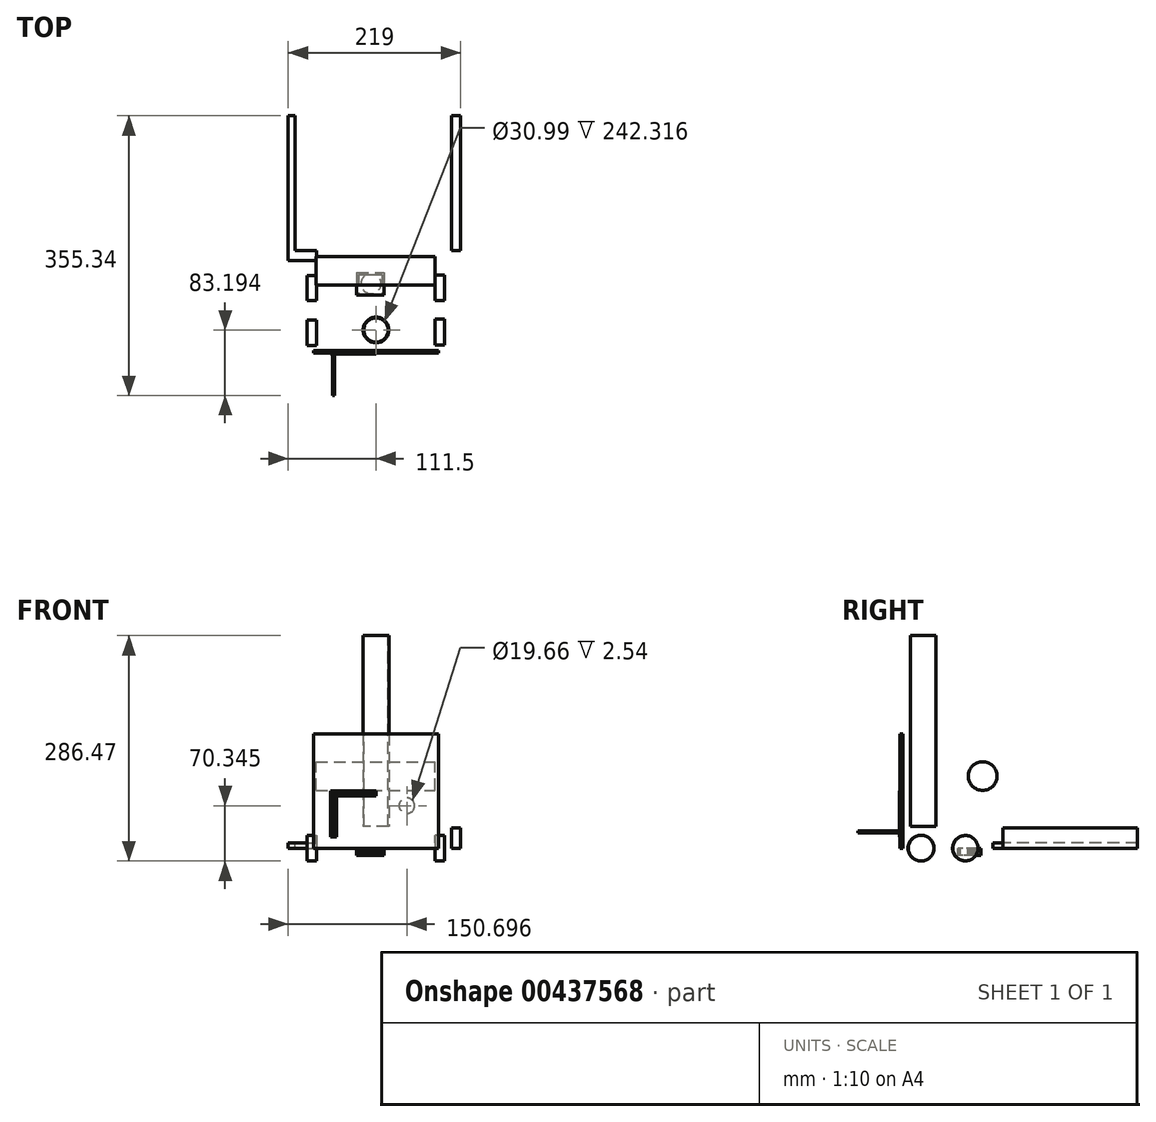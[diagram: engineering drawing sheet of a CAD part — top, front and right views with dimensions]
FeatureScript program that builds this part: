
annotation { "Feature Type Name" : "Feature", "Feature Type Description" : "" }
export const myFeature = defineFeature(function(context is Context, id is Id, definition is map)
    precondition{}
    {
        {
            var Q0;
            Q0=qCreatedBy(makeId("Front.planeOp"),FACE);
            var sketch = newSketch(context, id + "F0", { "sketchPlane" : qUnion([Q0])});
            skLineSegment(sketch, "E0.bottom", {"start": v(-79.55, 72.7) * mm, "end": v(79.55, 72.7) * mm});
            skLineSegment(sketch, "E0.top", {"start": v(-79.55, -72.7) * mm, "end": v(79.55, -72.7) * mm});
            skLineSegment(sketch, "E0.left", {"start": v(-79.55, 72.7) * mm, "end": v(-79.55, -72.7) * mm});
            skLineSegment(sketch, "E0.right", {"start": v(79.55, 72.7) * mm, "end": v(79.55, -72.7) * mm});
            skPoint(sketch, "E0.middle", {"position": v(0, 0) * mm});
            skSolve(sketch);
        }
        {
            var Q0;
            Q0=makeQuery(id+"F0.imprint","IMPRINT",FACE,{"disambiguationData":[TD([[makeQuery(id+"F0.imprint","IMPRINT",EDGE,{"derivedFrom":sQuery(id+"F0.wireOp",EDGE,"E0.bottom")}),-1.0]])]});
            extrude(context, id + "F1", {"entities" : qUnion([Q0]), "depth" : 3.56 * mm});
        }
        {
            var Q0;
            Q0=makeQuery(id+"F1.opExtrude","CAP_FACE",FACE,{"disambiguationData":[OSD([sQuery(id+"F0.wireOp",EDGE,"E0.bottom"),sQuery(id+"F0.wireOp",EDGE,"E0.top"),sQuery(id+"F0.wireOp",EDGE,"E0.left"),sQuery(id+"F0.wireOp",EDGE,"E0.right")])],"isStart":true});
            var sketch = newSketch(context, id + "F2", { "sketchPlane" : qUnion([Q0])});
            skLineSegment(sketch, "E1.bottom", {"start": v(-79.55, 72.7) * mm, "end": v(-74.99, 72.7) * mm});
            skLineSegment(sketch, "E1.top", {"start": v(-79.55, -72.7) * mm, "end": v(-74.99, -72.7) * mm});
            skLineSegment(sketch, "E1.left", {"start": v(-79.55, 72.7) * mm, "end": v(-79.55, -72.7) * mm});
            skLineSegment(sketch, "E1.right", {"start": v(-74.99, 72.7) * mm, "end": v(-74.99, -72.7) * mm});
            skSolve(sketch);
        }
        {
            var Q0;
            Q0=sQuery(id+"F2.wireOp",EDGE,"E1.right");
            extrude(context, id + "F3", {"bodyType" : ToolBodyType.SURFACE, "surfaceEntities" : qUnion([Q0]), "depth" : 127 * mm});
        }
        {
            var Q0;
            Q0=makeQuery(id+"F1.opExtrude","CAP_FACE",FACE,{"disambiguationData":[OSD([sQuery(id+"F0.wireOp",EDGE,"E0.bottom"),sQuery(id+"F0.wireOp",EDGE,"E0.top"),sQuery(id+"F0.wireOp",EDGE,"E0.left"),sQuery(id+"F0.wireOp",EDGE,"E0.right")])],"isStart":true});
            var sketch = newSketch(context, id + "F4", { "sketchPlane" : qUnion([Q0])});
            skLineSegment(sketch, "E2.bottom", {"start": v(79.55, 72.7) * mm, "end": v(75.43, 72.7) * mm});
            skLineSegment(sketch, "E2.top", {"start": v(79.55, -72.7) * mm, "end": v(75.43, -72.7) * mm});
            skLineSegment(sketch, "E2.left", {"start": v(79.55, 72.7) * mm, "end": v(79.55, -72.7) * mm});
            skLineSegment(sketch, "E2.right", {"start": v(75.43, 72.7) * mm, "end": v(75.43, -72.7) * mm});
            skSolve(sketch);
        }
        {
            var Q0;
            Q0=sQuery(id+"F4.wireOp",EDGE,"E2.right");
            extrude(context, id + "F5", {"bodyType" : ToolBodyType.SURFACE, "surfaceEntities" : qUnion([Q0]), "depth" : 127 * mm});
        }
        {
            var Q0;
            Q0=makeQuery(id+"F3.opExtrude","SWEPT_FACE",FACE,{"disambiguationData":[OSD([sQuery(id+"F2.wireOp",EDGE,"E1.right")])]});
            var sketch = newSketch(context, id + "F6", { "sketchPlane" : qUnion([Q0])});
            skCircle(sketch, "E3", {"center": v(101.22, 18.92) * mm, "radius": 18.2 * mm});
            skSolve(sketch);
        }
        {
            var Q0;
            Q0=makeQuery(id+"F6.imprint","IMPRINT",FACE,{"disambiguationData":[TD([[makeQuery(id+"F6.imprint","IMPRINT",EDGE,{"derivedFrom":sQuery(id+"F6.wireOp",EDGE,"E3")}),1.0]])]});
            extrude(context, id + "F7", {"entities" : qUnion([Q0]), "oppositeDirection" : true, "depth" : 151.38 * mm});
        }
        {
            var Q0;
            Q0=makeQuery(id+"F3.opExtrude","SWEPT_FACE",FACE,{"disambiguationData":[OSD([sQuery(id+"F2.wireOp",EDGE,"E1.right")])]});
            var sketch = newSketch(context, id + "F8", { "sketchPlane" : qUnion([Q0])});
            skLineSegment(sketch, "E4", {"start": v(127, -72.7) * mm, "end": v(55.42, -20.75) * mm});
            skSolve(sketch);
        }
        {
            var Q0;
            Q0=sQuery(id+"F8.wireOp",EDGE,"E4");
            extrude(context, id + "F9", {"bodyType" : ToolBodyType.SURFACE, "surfaceEntities" : qUnion([Q0]), "oppositeDirection" : true, "depth" : 150.11 * mm});
        }
        {
            var Q0;
            Q0=makeQuery(id+"F5.opExtrude","SWEPT_FACE",FACE,{"disambiguationData":[OSD([sQuery(id+"F4.wireOp",EDGE,"E2.right")])]});
            var sketch = newSketch(context, id + "F10", { "sketchPlane" : qUnion([Q0])});
            skLineSegment(sketch, "E5", {"start": v(88.54, -44.94) * mm, "end": v(0, -44.94) * mm});
            skSolve(sketch);
        }
        {
            var Q0;
            Q0=sQuery(id+"F10.wireOp",EDGE,"E5");
            extrude(context, id + "F11", {"bodyType" : ToolBodyType.SURFACE, "surfaceEntities" : qUnion([Q0]), "depth" : 143.5 * mm});
        }
        {
            var Q0;
            Q0=makeQuery(id+"F1.opExtrude","SWEPT_FACE",FACE,{"disambiguationData":[OSD([sQuery(id+"F0.wireOp",EDGE,"E0.top")])]});
            var sketch = newSketch(context, id + "F12", { "sketchPlane" : qUnion([Q0])});
            skLineSegment(sketch, "E6.bottom", {"start": v(79.55, 0) * mm, "end": v(-76.12, 0) * mm});
            skLineSegment(sketch, "E6.top", {"start": v(79.55, -126.38) * mm, "end": v(-76.12, -126.38) * mm});
            skLineSegment(sketch, "E6.left", {"start": v(79.55, 0) * mm, "end": v(79.55, -126.38) * mm});
            skLineSegment(sketch, "E6.right", {"start": v(-76.12, 0) * mm, "end": v(-76.12, -126.38) * mm});
            skSolve(sketch);
        }
        {
            var Q0;
            Q0=makeQuery(id+"F5.opExtrude","SWEPT_FACE",FACE,{"disambiguationData":[OSD([sQuery(id+"F4.wireOp",EDGE,"E2.right")])]});
            var sketch = newSketch(context, id + "F13", { "sketchPlane" : qUnion([Q0])});
            skLineSegment(sketch, "E7.bottom", {"start": v(127, -72.7) * mm, "end": v(114.2, -72.7) * mm});
            skLineSegment(sketch, "E7.top", {"start": v(127, -66.11) * mm, "end": v(114.2, -66.11) * mm});
            skLineSegment(sketch, "E7.left", {"start": v(127, -72.7) * mm, "end": v(127, -66.11) * mm});
            skLineSegment(sketch, "E7.right", {"start": v(114.2, -72.7) * mm, "end": v(114.2, -66.11) * mm});
            skSolve(sketch);
        }
        {
            var Q0;
            Q0=makeQuery(id+"F13.imprint","IMPRINT",FACE,{"disambiguationData":[TD([[makeQuery(id+"F13.imprint","IMPRINT",EDGE,{"derivedFrom":sQuery(id+"F13.wireOp",EDGE,"E7.bottom")}),1.0]])]});
            extrude(context, id + "F14", {"entities" : qUnion([Q0]), "oppositeDirection" : true, "depth" : 36.07 * mm});
        }
        {
            var Q0;
            Q0=makeQuery(id+"F14.opExtrude","SWEPT_FACE",FACE,{"disambiguationData":[OSD([sQuery(id+"F13.wireOp",EDGE,"E7.left")])]});
            var sketch = newSketch(context, id + "F15", { "sketchPlane" : qUnion([Q0])});
            skLineSegment(sketch, "E8.bottom", {"start": v(111.5, -72.7) * mm, "end": v(102.88, -72.7) * mm});
            skLineSegment(sketch, "E8.top", {"start": v(111.5, -66.11) * mm, "end": v(102.88, -66.11) * mm});
            skLineSegment(sketch, "E8.left", {"start": v(111.5, -72.7) * mm, "end": v(111.5, -66.11) * mm});
            skLineSegment(sketch, "E8.right", {"start": v(102.88, -72.7) * mm, "end": v(102.88, -66.11) * mm});
            skSolve(sketch);
        }
        {
            var Q0;
            Q0=makeQuery(id+"F15.imprint","IMPRINT",FACE,{"disambiguationData":[TD([[makeQuery(id+"F15.imprint","IMPRINT",EDGE,{"derivedFrom":sQuery(id+"F15.wireOp",EDGE,"E8.bottom")}),-1.0]])]});
            extrude(context, id + "F16", {"entities" : qUnion([Q0]), "operationType" : NewBodyOperationType.ADD, "depth" : 170.94 * mm});
        }
        {
            var Q0;
            Q0=makeQuery(id+"F16.boolean.opBoolean","MERGE",FACE,{"derivedFrom":[makeQuery(id+"F14.opExtrude","SWEPT_FACE",FACE,{"disambiguationData":[OSD([sQuery(id+"F13.wireOp",EDGE,"E7.top")])]}),makeQuery(id+"F16.opExtrude","SWEPT_FACE",FACE,{"disambiguationData":[OSD([sQuery(id+"F15.wireOp",EDGE,"E8.top")])]})]});
            var sketch = newSketch(context, id + "F17", { "sketchPlane" : qUnion([Q0])});
            skCircle(sketch, "E9", {"center": v(-105.59, 120.53) * mm, "radius": 2.71 * mm});
            skSolve(sketch);
        }
        {
            var Q0;
            Q0=makeQuery(id+"F1.opExtrude","CAP_FACE",FACE,{"disambiguationData":[OSD([sQuery(id+"F0.wireOp",EDGE,"E0.bottom"),sQuery(id+"F0.wireOp",EDGE,"E0.top"),sQuery(id+"F0.wireOp",EDGE,"E0.left"),sQuery(id+"F0.wireOp",EDGE,"E0.right")])],"isStart":false});
            var sketch = newSketch(context, id + "F18", { "sketchPlane" : qUnion([Q0])});
            skCircle(sketch, "E10", {"center": v(39.2, -18.75) * mm, "radius": 9.83 * mm});
            skSolve(sketch);
        }
        {
            var Q0;
            Q0 = qSketchRegion(id + "F18", true);
            extrude(context, id + "F19", {"entities" : qUnion([Q0]), "operationType" : NewBodyOperationType.REMOVE, "oppositeDirection" : true, "depth" : 25.4 * mm});
        }
        {
            var Q0;
            Q0=makeQuery(id+"F1.opExtrude","CAP_FACE",FACE,{"disambiguationData":[OSD([sQuery(id+"F0.wireOp",EDGE,"E0.bottom"),sQuery(id+"F0.wireOp",EDGE,"E0.top"),sQuery(id+"F0.wireOp",EDGE,"E0.left"),sQuery(id+"F0.wireOp",EDGE,"E0.right")])],"isStart":false});
            var sketch = newSketch(context, id + "F20", { "sketchPlane" : qUnion([Q0])});
            skCircle(sketch, "E11", {"center": v(39.2, -18.75) * mm, "radius": 9.94 * mm});
            skSolve(sketch);
        }
        {
            var Q0;
            Q0 = qSketchRegion(id + "F20", true);
            extrude(context, id + "F21", {"entities" : qUnion([Q0]), "operationType" : NewBodyOperationType.ADD, "oppositeDirection" : true, "depth" : 1.02 * mm});
        }
        {
            var Q0;
            Q0=makeQuery(id+"F3.opExtrude","SWEPT_FACE",FACE,{"disambiguationData":[OSD([sQuery(id+"F2.wireOp",EDGE,"E1.right")])]});
            var sketch = newSketch(context, id + "F22", { "sketchPlane" : qUnion([Q0])});
            skLineSegment(sketch, "E12.bottom", {"start": v(127, -72.7) * mm, "end": v(117.95, -72.7) * mm});
            skLineSegment(sketch, "E12.top", {"start": v(127, -65.87) * mm, "end": v(117.95, -65.87) * mm});
            skLineSegment(sketch, "E12.left", {"start": v(127, -72.7) * mm, "end": v(127, -65.87) * mm});
            skLineSegment(sketch, "E12.right", {"start": v(117.95, -72.7) * mm, "end": v(117.95, -65.87) * mm});
            skSolve(sketch);
        }
        {
            var Q0;
            Q0=sQuery(id+"F22.wireOp",EDGE,"E12.bottom");
            var Q1;
            Q1=sQuery(id+"F22.wireOp",EDGE,"E12.top");
            var Q2;
            Q2=sQuery(id+"F22.wireOp",EDGE,"E12.right");
            var Q3;
            Q3=sQuery(id+"F22.wireOp",EDGE,"E12.left");
            extrude(context, id + "F23", {"bodyType" : ToolBodyType.SURFACE, "surfaceEntities" : qUnion([Q0, Q1, Q2, Q3]), "depth" : 32.5 * mm});
        }
        {
            var Q0;
            Q0=makeQuery(id+"F23.opExtrude","SWEPT_FACE",FACE,{"disambiguationData":[OSD([sQuery(id+"F22.wireOp",EDGE,"E12.left")])]});
            var sketch = newSketch(context, id + "F24", { "sketchPlane" : qUnion([Q0])});
            skLineSegment(sketch, "E13.bottom", {"start": v(107.5, -72.7) * mm, "end": v(96.1, -72.7) * mm});
            skLineSegment(sketch, "E13.top", {"start": v(107.5, -65.87) * mm, "end": v(96.1, -65.87) * mm});
            skLineSegment(sketch, "E13.left", {"start": v(107.5, -72.7) * mm, "end": v(107.5, -65.87) * mm});
            skLineSegment(sketch, "E13.right", {"start": v(96.1, -72.7) * mm, "end": v(96.1, -65.87) * mm});
            skSolve(sketch);
        }
        {
            var Q0;
            Q0 = qSketchRegion(id + "F24", true);
            extrude(context, id + "F25", {"entities" : qUnion([Q0]), "oppositeDirection" : true, "depth" : 170.94 * mm});
        }
        {
            var Q0;
            Q0=makeQuery(id+"F11.opExtrude","SWEPT_FACE",FACE,{"disambiguationData":[OSD([sQuery(id+"F10.wireOp",EDGE,"E5")])]});
            var sketch = newSketch(context, id + "F26", { "sketchPlane" : qUnion([Q0])});
            skCircle(sketch, "E14", {"center": v(0, 25.8) * mm, "radius": 16.3 * mm});
            skSolve(sketch);
        }
        {
            var Q0;
            Q0=makeQuery(id+"F26.imprint","IMPRINT",FACE,{"disambiguationData":[TD([[makeQuery(id+"F26.imprint","IMPRINT",EDGE,{"derivedFrom":sQuery(id+"F26.wireOp",EDGE,"E14")}),1.0]])]});
            extrude(context, id + "F27", {"entities" : qUnion([Q0]), "depth" : 242.32 * mm});
        }
        {
            var Q0;
            Q0=makeQuery(id+"F27.opExtrude","CAP_FACE",FACE,{"disambiguationData":[OSD([sQuery(id+"F26.wireOp",EDGE,"E14")])],"isStart":false});
            var sketch = newSketch(context, id + "F28", { "sketchPlane" : qUnion([Q0])});
            skCircle(sketch, "E15", {"center": v(0, 25.8) * mm, "radius": 15.5 * mm});
            skSolve(sketch);
        }
        {
            var Q0;
            Q0=makeQuery(id+"F28.imprint","IMPRINT",FACE,{"disambiguationData":[TD([[makeQuery(id+"F28.imprint","IMPRINT",EDGE,{"derivedFrom":sQuery(id+"F28.wireOp",EDGE,"E15")}),1.0]])]});
            extrude(context, id + "F29", {"entities" : qUnion([Q0]), "operationType" : NewBodyOperationType.REMOVE, "oppositeDirection" : true, "depth" : 245.87 * mm});
        }
        {
            var Q0;
            Q0=makeQuery(id+"F5.opExtrude","SWEPT_FACE",FACE,{"disambiguationData":[OSD([sQuery(id+"F4.wireOp",EDGE,"E2.right")])]});
            var sketch = newSketch(context, id + "F30", { "sketchPlane" : qUnion([Q0])});
            skCircle(sketch, "E16", {"center": v(22.38, -72.7) * mm, "radius": 16.06 * mm});
            skCircle(sketch, "E17", {"center": v(79.03, -72.7) * mm, "radius": 16.04 * mm});
            skSolve(sketch);
        }
        {
            var Q0;
            {var subQ0=sQuery(id+"F30.wireOp",EDGE,"E17");var subQ1=makeQuery(id+"F5.opExtrude","SWEPT_EDGE",EDGE,{"disambiguationData":[OSD([sQuery(id+"F4.wireOp",VERTEX,"E2.right.end")])]});var subQ2=makeQuery(id+"F30.imprint","INTERSECT",VERTEX,{"disambiguationData":[OD(0.0)],"derivedFrom":[subQ1,subQ0]});Q0=makeQuery(id+"F30.imprint","IMPRINT",FACE,{"disambiguationData":[TD([[makeQuery(id+"F30.imprint","IMPRINT",EDGE,{"disambiguationData":[TD([[subQ2,1.0]])],"derivedFrom":subQ0}),1.0]])]});}
            var Q1;
            {var subQ0=sQuery(id+"F30.wireOp",EDGE,"E17");var subQ1=makeQuery(id+"F5.opExtrude","SWEPT_EDGE",EDGE,{"disambiguationData":[OSD([sQuery(id+"F4.wireOp",VERTEX,"E2.right.end")])]});var subQ2=makeQuery(id+"F30.imprint","INTERSECT",VERTEX,{"disambiguationData":[OD(0.0)],"derivedFrom":[subQ1,subQ0]});Q1=makeQuery(id+"F30.imprint","IMPRINT",FACE,{"disambiguationData":[TD([[makeQuery(id+"F30.imprint","IMPRINT",EDGE,{"disambiguationData":[TD([[subQ2,-1.0]])],"derivedFrom":subQ0}),1.0]])]});}
            var Q2;
            {var subQ0=sQuery(id+"F30.wireOp",EDGE,"E16");var subQ1=makeQuery(id+"F5.opExtrude","SWEPT_EDGE",EDGE,{"disambiguationData":[OSD([sQuery(id+"F4.wireOp",VERTEX,"E2.right.end")])]});var subQ2=makeQuery(id+"F30.imprint","INTERSECT",VERTEX,{"disambiguationData":[OD(0.0)],"derivedFrom":[subQ1,subQ0]});Q2=makeQuery(id+"F30.imprint","IMPRINT",FACE,{"disambiguationData":[TD([[makeQuery(id+"F30.imprint","IMPRINT",EDGE,{"disambiguationData":[TD([[subQ2,1.0]])],"derivedFrom":subQ0}),1.0]])]});}
            var Q3;
            {var subQ0=sQuery(id+"F30.wireOp",EDGE,"E16");var subQ1=makeQuery(id+"F5.opExtrude","SWEPT_EDGE",EDGE,{"disambiguationData":[OSD([sQuery(id+"F4.wireOp",VERTEX,"E2.right.end")])]});var subQ2=makeQuery(id+"F30.imprint","INTERSECT",VERTEX,{"disambiguationData":[OD(0.0)],"derivedFrom":[subQ1,subQ0]});Q3=makeQuery(id+"F30.imprint","IMPRINT",FACE,{"disambiguationData":[TD([[makeQuery(id+"F30.imprint","IMPRINT",EDGE,{"disambiguationData":[TD([[subQ2,-1.0]])],"derivedFrom":subQ0}),1.0]])]});}
            extrude(context, id + "F31", {"entities" : qUnion([Q0, Q1, Q2, Q3]), "oppositeDirection" : true, "depth" : 12.2 * mm});
        }
        {
            var Q0;
            Q0=makeQuery(id+"F3.opExtrude","SWEPT_FACE",FACE,{"disambiguationData":[OSD([sQuery(id+"F2.wireOp",EDGE,"E1.right")])]});
            var sketch = newSketch(context, id + "F32", { "sketchPlane" : qUnion([Q0])});
            skCircle(sketch, "E18", {"center": v(23.08, -72.7) * mm, "radius": 16.4 * mm});
            skCircle(sketch, "E19", {"center": v(79.41, -72.7) * mm, "radius": 16.02 * mm});
            skSolve(sketch);
        }
        {
            var Q0;
            {var subQ0=sQuery(id+"F32.wireOp",EDGE,"E18");var subQ1=makeQuery(id+"F3.opExtrude","SWEPT_EDGE",EDGE,{"disambiguationData":[OSD([sQuery(id+"F2.wireOp",VERTEX,"E1.right.end")])]});var subQ2=makeQuery(id+"F32.imprint","INTERSECT",VERTEX,{"disambiguationData":[OD(0.0)],"derivedFrom":[subQ1,subQ0]});Q0=makeQuery(id+"F32.imprint","IMPRINT",FACE,{"disambiguationData":[TD([[makeQuery(id+"F32.imprint","IMPRINT",EDGE,{"disambiguationData":[TD([[subQ2,-1.0]])],"derivedFrom":subQ0}),1.0]])]});}
            var Q1;
            {var subQ0=sQuery(id+"F32.wireOp",EDGE,"E18");var subQ1=makeQuery(id+"F3.opExtrude","SWEPT_EDGE",EDGE,{"disambiguationData":[OSD([sQuery(id+"F2.wireOp",VERTEX,"E1.right.end")])]});var subQ2=makeQuery(id+"F32.imprint","INTERSECT",VERTEX,{"disambiguationData":[OD(0.0)],"derivedFrom":[subQ1,subQ0]});Q1=makeQuery(id+"F32.imprint","IMPRINT",FACE,{"disambiguationData":[TD([[makeQuery(id+"F32.imprint","IMPRINT",EDGE,{"disambiguationData":[TD([[subQ2,1.0]])],"derivedFrom":subQ0}),1.0]])]});}
            var Q2;
            {var subQ0=sQuery(id+"F32.wireOp",EDGE,"E19");var subQ1=makeQuery(id+"F3.opExtrude","SWEPT_EDGE",EDGE,{"disambiguationData":[OSD([sQuery(id+"F2.wireOp",VERTEX,"E1.right.end")])]});var subQ2=makeQuery(id+"F32.imprint","INTERSECT",VERTEX,{"disambiguationData":[OD(0.0)],"derivedFrom":[subQ1,subQ0]});Q2=makeQuery(id+"F32.imprint","IMPRINT",FACE,{"disambiguationData":[TD([[makeQuery(id+"F32.imprint","IMPRINT",EDGE,{"disambiguationData":[TD([[subQ2,1.0]])],"derivedFrom":subQ0}),1.0]])]});}
            var Q3;
            {var subQ0=sQuery(id+"F32.wireOp",EDGE,"E19");var subQ1=makeQuery(id+"F3.opExtrude","SWEPT_EDGE",EDGE,{"disambiguationData":[OSD([sQuery(id+"F2.wireOp",VERTEX,"E1.right.end")])]});var subQ2=makeQuery(id+"F32.imprint","INTERSECT",VERTEX,{"disambiguationData":[OD(0.0)],"derivedFrom":[subQ1,subQ0]});Q3=makeQuery(id+"F32.imprint","IMPRINT",FACE,{"disambiguationData":[TD([[makeQuery(id+"F32.imprint","IMPRINT",EDGE,{"disambiguationData":[TD([[subQ2,-1.0]])],"derivedFrom":subQ0}),1.0]])]});}
            extrude(context, id + "F33", {"entities" : qUnion([Q0, Q1, Q2, Q3]), "depth" : 12.2 * mm});
        }
        {
            var Q0;
            Q0=makeQuery(id+"F12.imprint","IMPRINT",FACE,{"disambiguationData":[TD([[makeQuery(id+"F12.imprint","IMPRINT",EDGE,{"derivedFrom":sQuery(id+"F12.wireOp",EDGE,"E6.bottom")}),-1.0]])]});
            var sketch = newSketch(context, id + "F34", { "sketchPlane" : qUnion([Q0])});
            skLineSegment(sketch, "E20.bottom", {"start": v(-24.52, -99) * mm, "end": v(10.44, -99) * mm});
            skLineSegment(sketch, "E20.top", {"start": v(-24.52, -70.02) * mm, "end": v(10.44, -70.02) * mm});
            skLineSegment(sketch, "E20.left", {"start": v(-24.52, -99) * mm, "end": v(-24.52, -70.02) * mm});
            skLineSegment(sketch, "E20.right", {"start": v(10.44, -99) * mm, "end": v(10.44, -70.02) * mm});
            skSolve(sketch);
        }
        {
            var Q0;
            Q0 = qSketchRegion(id + "F34", true);
            extrude(context, id + "F35", {"entities" : qUnion([Q0]), "depth" : 9.14 * mm});
        }
        {
            var Q0;
            Q0=makeQuery(id+"F35.opExtrude","SWEPT_FACE",FACE,{"disambiguationData":[OSD([sQuery(id+"F34.wireOp",EDGE,"E20.top")])]});
            shell(context, id + "F36", {"entities" : qUnion([Q0]), "thickness" : 2.54 * mm});
        }
        {
            var Q0;
            {var subQ0=sQuery(id+"F34.wireOp",EDGE,"E20.right");var subQ1=sQuery(id+"F34.wireOp",EDGE,"E20.left");var subQ2=sQuery(id+"F34.wireOp",EDGE,"E20.top");var subQ3=sQuery(id+"F34.wireOp",EDGE,"E20.bottom");Q0=makeQuery(id+"F36.opShell","OFFSET_FACE",FACE,{"disambiguationData":[OSD([subQ3,subQ2,subQ1,subQ0]),TDD([makeQuery(id+"F35.opExtrude","CAP_FACE",FACE,{"disambiguationData":[OSD([subQ3,subQ2,subQ1,subQ0])],"isStart":true})])]});}
            var sketch = newSketch(context, id + "F37", { "sketchPlane" : qUnion([Q0])});
            skCircle(sketch, "E21", {"center": v(-6.25, -84.8) * mm, "radius": 12.8 * mm});
            skSolve(sketch);
        }
        {
            var Q0;
            Q0 = qSketchRegion(id + "F37", true);
            extrude(context, id + "F38", {"entities" : qUnion([Q0]), "operationType" : NewBodyOperationType.ADD, "depth" : 3.05 * mm});
        }
        {
            var Q0;
            Q0=makeQuery(id+"F25.opExtrude","SWEPT_FACE",FACE,{"disambiguationData":[OSD([sQuery(id+"F24.wireOp",EDGE,"E13.top")])]});
            var sketch = newSketch(context, id + "F39", { "sketchPlane" : qUnion([Q0])});
            skLineSegment(sketch, "E22.bottom", {"start": v(96.1, 297.94) * mm, "end": v(107.5, 297.94) * mm});
            skLineSegment(sketch, "E22.top", {"start": v(96.1, 127) * mm, "end": v(107.5, 127) * mm});
            skLineSegment(sketch, "E22.left", {"start": v(96.1, 297.94) * mm, "end": v(96.1, 127) * mm});
            skLineSegment(sketch, "E22.right", {"start": v(107.5, 297.94) * mm, "end": v(107.5, 127) * mm});
            skSolve(sketch);
        }
        {
            var Q0;
            Q0=makeQuery(id+"F39.imprint","IMPRINT",FACE,{"disambiguationData":[TD([[makeQuery(id+"F39.imprint","IMPRINT",EDGE,{"derivedFrom":sQuery(id+"F39.wireOp",EDGE,"E22.bottom")}),-1.0]])]});
            extrude(context, id + "F40", {"entities" : qUnion([Q0]), "operationType" : NewBodyOperationType.ADD, "depth" : 19.05 * mm});
        }
        {
            var Q0;
            Q0=makeQuery(id+"F17.imprint","IMPRINT",FACE,{"disambiguationData":[TD([[makeQuery(id+"F17.imprint","IMPRINT",EDGE,{"derivedFrom":sQuery(id+"F17.wireOp",EDGE,"E9")}),-1.0]])]});
            var sketch = newSketch(context, id + "F41", { "sketchPlane" : qUnion([Q0])});
            skLineSegment(sketch, "E23.bottom", {"start": v(-111.56, 297.83) * mm, "end": v(-102.49, 297.83) * mm});
            skLineSegment(sketch, "E23.top", {"start": v(-111.56, 127.4) * mm, "end": v(-102.49, 127.4) * mm});
            skLineSegment(sketch, "E23.left", {"start": v(-111.56, 297.83) * mm, "end": v(-111.56, 127.4) * mm});
            skLineSegment(sketch, "E23.right", {"start": v(-102.49, 297.83) * mm, "end": v(-102.49, 127.4) * mm});
            skSolve(sketch);
        }
        {
            var Q0;
            Q0=sQuery(id+"F41.wireOp",EDGE,"E23.top");
            var Q1;
            Q1=sQuery(id+"F41.wireOp",EDGE,"E23.left");
            var Q2;
            Q2=sQuery(id+"F41.wireOp",EDGE,"E23.right");
            var Q3;
            Q3=sQuery(id+"F41.wireOp",EDGE,"E23.bottom");
            extrude(context, id + "F42", {"bodyType" : ToolBodyType.SURFACE, "surfaceEntities" : qUnion([Q0, Q1, Q2, Q3]), "depth" : 18.03 * mm});
        }
        {
            var Q0;
            Q0=makeQuery(id+"F21.boolean.opBoolean","MERGE",FACE,{"derivedFrom":[makeQuery(id+"F1.opExtrude","CAP_FACE",FACE,{"disambiguationData":[OSD([sQuery(id+"F0.wireOp",EDGE,"E0.bottom"),sQuery(id+"F0.wireOp",EDGE,"E0.top"),sQuery(id+"F0.wireOp",EDGE,"E0.left"),sQuery(id+"F0.wireOp",EDGE,"E0.right")])],"isStart":false}),makeQuery(id+"F21.opExtrude","CAP_FACE",FACE,{"disambiguationData":[OSD([sQuery(id+"F20.wireOp",EDGE,"E11")])],"isStart":true})]});
            var sketch = newSketch(context, id + "F43", { "sketchPlane" : qUnion([Q0])});
            skLineSegment(sketch, "E24.bottom", {"start": v(-57.8, -58.1) * mm, "end": v(-50.12, -58.1) * mm});
            skLineSegment(sketch, "E24.top", {"start": v(-57.8, 0) * mm, "end": v(-50.12, 0) * mm});
            skLineSegment(sketch, "E24.left", {"start": v(-57.8, -58.1) * mm, "end": v(-57.8, 0) * mm});
            skLineSegment(sketch, "E24.right", {"start": v(-50.12, -58.1) * mm, "end": v(-50.12, 0) * mm});
            skLineSegment(sketch, "E25.bottom", {"start": v(-50.12, 0) * mm, "end": v(0, 0) * mm});
            skLineSegment(sketch, "E25.top", {"start": v(-50.12, -6.58) * mm, "end": v(0, -6.58) * mm});
            skLineSegment(sketch, "E25.left", {"start": v(-50.12, 0) * mm, "end": v(-50.12, -6.58) * mm});
            skLineSegment(sketch, "E25.right", {"start": v(0, 0) * mm, "end": v(0, -6.58) * mm});
            skSolve(sketch);
        }
        {
            var Q0;
            Q0=makeQuery(id+"F43.imprint","IMPRINT",FACE,{"disambiguationData":[TD([[makeQuery(id+"F43.imprint","IMPRINT",EDGE,{"derivedFrom":sQuery(id+"F43.wireOp",EDGE,"E24.bottom")}),1.0]])]});
            var Q1;
            Q1=makeQuery(id+"F43.imprint","IMPRINT",FACE,{"disambiguationData":[TD([[makeQuery(id+"F43.imprint","IMPRINT",EDGE,{"derivedFrom":sQuery(id+"F43.wireOp",EDGE,"E25.bottom")}),-1.0]])]});
            extrude(context, id + "F44", {"entities" : qUnion([Q0, Q1]), "operationType" : NewBodyOperationType.ADD, "depth" : 1.02 * mm});
        }
        {
            var Q0;
            Q0=makeQuery(id+"F44.opExtrude","CAP_FACE",FACE,{"disambiguationData":[OSD([sQuery(id+"F43.wireOp",EDGE,"E24.bottom"),sQuery(id+"F43.wireOp",EDGE,"E24.top"),sQuery(id+"F43.wireOp",EDGE,"E24.left"),sQuery(id+"F43.wireOp",EDGE,"E24.right"),sQuery(id+"F43.wireOp",EDGE,"E25.bottom"),sQuery(id+"F43.wireOp",EDGE,"E25.top"),sQuery(id+"F43.wireOp",EDGE,"E25.right")])],"isStart":false});
            shell(context, id + "F45", {"entities" : qUnion([Q0]), "thickness" : 2.54 * mm});
        }
        {
            var Q0;
            Q0=makeQuery(id+"F45.opShell","OFFSET_FACE",FACE,{"disambiguationData":[OSD([sQuery(id+"F0.wireOp",EDGE,"E0.bottom"),sQuery(id+"F0.wireOp",EDGE,"E0.top"),sQuery(id+"F0.wireOp",EDGE,"E0.left"),sQuery(id+"F0.wireOp",EDGE,"E0.right")])]});
            var sketch = newSketch(context, id + "F46", { "sketchPlane" : qUnion([Q0])});
            skCircle(sketch, "E26", {"center": v(-54.05, -52.23) * mm, "radius": 1.22 * mm});
            skSolve(sketch);
        }
        {
            var Q0;
            Q0 = qSketchRegion(id + "F46", true);
            extrude(context, id + "F47", {"entities" : qUnion([Q0]), "operationType" : NewBodyOperationType.ADD, "depth" : 54.86 * mm});
        }
    });
